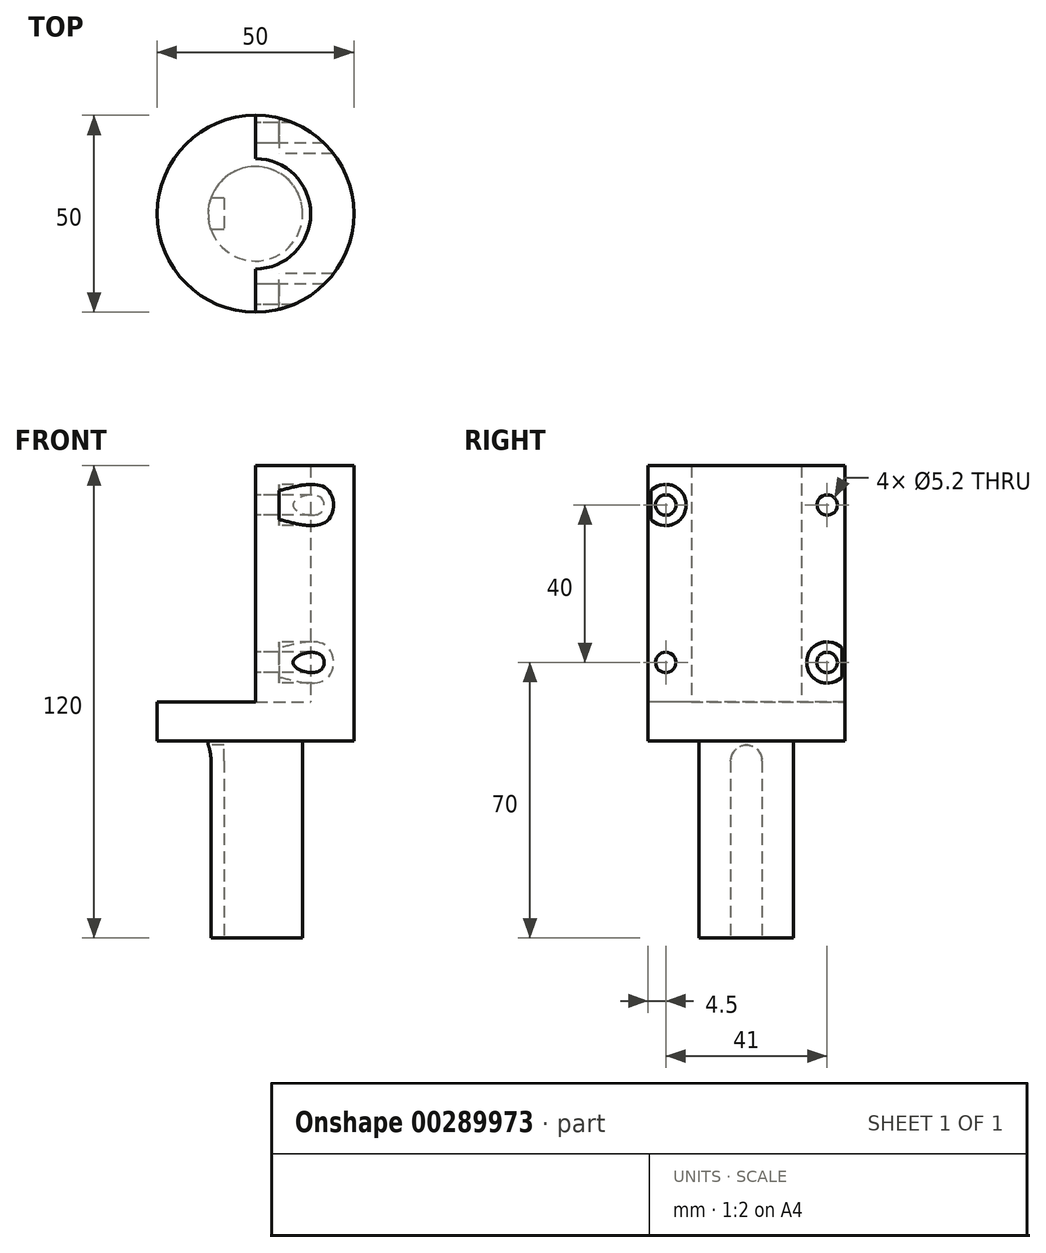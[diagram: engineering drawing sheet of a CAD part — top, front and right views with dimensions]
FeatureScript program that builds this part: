
annotation { "Feature Type Name" : "Feature", "Feature Type Description" : "" }
export const myFeature = defineFeature(function(context is Context, id is Id, definition is map)
    precondition{}
    {
        {
            var Q0;
            Q0=qCreatedBy(makeId("Top.planeOp"),FACE);
            var sketch = newSketch(context, id + "F0", { "sketchPlane" : qUnion([Q0])});
            skCircle(sketch, "E0", {"center": v(0, 0) * mm, "radius": 12 * mm});
            skSolve(sketch);
        }
        {
            var Q0;
            Q0=qSketchRegion(id+"F0",true);
            extrude(context, id + "F1", {"entities" : qUnion([Q0]), "depth" : 50 * mm});
        }
        {
            var Q0;
            Q0=makeQuery(id+"F1.opExtrude","CAP_FACE",FACE,{"disambiguationData":[OSD([sQuery(id+"F0.wireOp",EDGE,"E0")])],"isStart":false});
            var sketch = newSketch(context, id + "F2", { "sketchPlane" : qUnion([Q0])});
            skCircle(sketch, "E1", {"center": v(0, 0) * mm, "radius": 25 * mm});
            skSolve(sketch);
        }
        {
            var Q0;
            Q0=qSketchRegion(id+"F2",true);
            extrude(context, id + "F3", {"entities" : qUnion([Q0]), "operationType" : NewBodyOperationType.ADD, "depth" : 10 * mm});
        }
        {
            var Q0;
            Q0=makeQuery(id+"F3.opExtrude","CAP_FACE",FACE,{"disambiguationData":[OSD([sQuery(id+"F2.wireOp",EDGE,"E1")])],"isStart":false});
            var sketch = newSketch(context, id + "F4", { "sketchPlane" : qUnion([Q0])});
            skArc(sketch, "E2", {"start": v(0, -14) * mm, "mid": v(14, 0) * mm, "end": v(0, 14) * mm});
            skArc(sketch, "E3", {"start": v(0, -25) * mm, "mid": v(25, 0) * mm, "end": v(0, 25) * mm});
            skLineSegment(sketch, "E4", {"start": v(0, 14) * mm, "end": v(0, 25) * mm});
            skLineSegment(sketch, "E5", {"start": v(0, -14) * mm, "end": v(0, -25) * mm});
            skSolve(sketch);
        }
        {
            var Q0;
            Q0=makeQuery(id+"F4.imprint","IMPRINT",FACE,{"disambiguationData":[TD([[makeQuery(id+"F4.imprint","IMPRINT",EDGE,{"derivedFrom":sQuery(id+"F4.wireOp",EDGE,"E2")}),-1.0]])]});
            extrude(context, id + "F5", {"entities" : qUnion([Q0]), "operationType" : NewBodyOperationType.ADD, "depth" : 60 * mm});
        }
        {
            var Q0;
            Q0=makeQuery(id+"F5.opExtrude","SWEPT_FACE",FACE,{"disambiguationData":[OSD([sQuery(id+"F4.wireOp",EDGE,"E5")])]});
            var sketch = newSketch(context, id + "F6", { "sketchPlane" : qUnion([Q0])});
            skCircle(sketch, "E6", {"center": v(20.5, 70) * mm, "radius": 2.6 * mm});
            skCircle(sketch, "E7", {"center": v(20.5, 110) * mm, "radius": 2.6 * mm});
            skCircle(sketch, "E8", {"center": v(-20.5, 110) * mm, "radius": 2.6 * mm});
            skCircle(sketch, "E9", {"center": v(-20.5, 70) * mm, "radius": 2.6 * mm});
            skSolve(sketch);
        }
        {
            var Q0;
            Q0=qSketchRegion(id+"F6",true);
            extrude(context, id + "F7", {"entities" : qUnion([Q0]), "operationType" : NewBodyOperationType.REMOVE, "endBound" : BoundingType.THROUGH_ALL, "oppositeDirection" : true, "depth" : 25 * mm});
        }
        {
            var Q0;
            Q0=makeQuery(id+"F5.opExtrude","SWEPT_FACE",FACE,{"disambiguationData":[OSD([sQuery(id+"F4.wireOp",EDGE,"E5")])]});
            cPlane(context, id + "F8", {"entities" : qUnion([Q0]), "cplaneType" : CPlaneType.OFFSET, "offset" : 6 * mm, "oppositeDirection" : true, "width" : 150 * mm, "height" : 150 * mm});
        }
        {
            var Q0;
            Q0=qCreatedBy(id+"F8.planeOp",FACE);
            var sketch = newSketch(context, id + "F9", { "sketchPlane" : qUnion([Q0])});
            skCircle(sketch, "E10", {"center": v(20.5, 110) * mm, "radius": 5.25 * mm});
            skLineSegment(sketch, "E11", {"start": v(20.5, 110) * mm, "end": v(20.5, 70) * mm});
            skLineSegment(sketch, "E12", {"start": v(20.5, 70) * mm, "end": v(-20.5, 70) * mm});
            skCircle(sketch, "E13", {"center": v(-20.5, 70) * mm, "radius": 5.25 * mm});
            skSolve(sketch);
        }
        {
            var Q0;
            Q0=qSketchRegion(id+"F9",true);
            extrude(context, id + "F10", {"entities" : qUnion([Q0]), "operationType" : NewBodyOperationType.REMOVE, "oppositeDirection" : true, "depth" : 25 * mm});
        }
        {
            var Q0;
            Q0=makeQuery(id+"F1.opExtrude","CAP_FACE",FACE,{"disambiguationData":[OSD([sQuery(id+"F0.wireOp",EDGE,"E0")])],"isStart":true});
            var sketch = newSketch(context, id + "F11", { "sketchPlane" : qUnion([Q0])});
            skLineSegment(sketch, "E14.bottom", {"start": v(-8, -4) * mm, "end": v(-15, -4) * mm});
            skLineSegment(sketch, "E14.top", {"start": v(-8, 4) * mm, "end": v(-15, 4) * mm});
            skLineSegment(sketch, "E14.left", {"start": v(-8, -4) * mm, "end": v(-8, 4) * mm});
            skLineSegment(sketch, "E14.right", {"start": v(-15, -4) * mm, "end": v(-15, 4) * mm});
            skSolve(sketch);
        }
        {
            var Q0;
            Q0=qSketchRegion(id+"F11",true);
            extrude(context, id + "F12", {"entities" : qUnion([Q0]), "operationType" : NewBodyOperationType.REMOVE, "oppositeDirection" : true, "depth" : 45 * mm});
        }
        {
            var Q0;
            Q0=qCreatedBy(makeId("Right.planeOp"),FACE);
            cPlane(context, id + "F13", {"entities" : qUnion([Q0]), "cplaneType" : CPlaneType.OFFSET, "offset" : 12 * mm, "oppositeDirection" : true, "width" : 150 * mm, "height" : 150 * mm});
        }
        {
            var Q0;
            Q0=qCreatedBy(id+"F13.planeOp",FACE);
            var sketch = newSketch(context, id + "F14", { "sketchPlane" : qUnion([Q0])});
            skLineSegment(sketch, "E15", {"start": v(0, 0) * mm, "end": v(0, 45) * mm});
            skCircle(sketch, "E16", {"center": v(0, 45) * mm, "radius": 4 * mm});
            skSolve(sketch);
        }
        {
            var Q0;
            Q0 = qSketchRegion(id + "F14", true);
            extrude(context, id + "F15", {"entities" : qUnion([Q0]), "operationType" : NewBodyOperationType.REMOVE, "depth" : 4 * mm});
        }
    });
